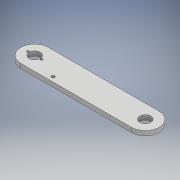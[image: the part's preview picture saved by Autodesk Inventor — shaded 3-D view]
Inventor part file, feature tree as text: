
AUTODESK INVENTOR PART (.ipt)
format: ipt  version: 2018.3 (Build 223284000, 284)  size: 119,808 bytes
history: native  units: mm
features: extrude x3, sketch x3
ambient origin geometry x8: Origin, YZ Plane, XZ Plane, XY Plane, X Axis, Y Axis, Z Axis, Center Point
bodies: Solid1 (feature_tree)
feature tree (6):
  extrude  "Extrusion1"  Depth=30.0mm
  extrude  "Extrusion2"  Depth=5.0mm TaperAngle=0.0deg
  extrude  "Extrusion3"  Depth=10.0mm
  sketch  "Sketch1"  dims[d0=12.0mm d1=30.0mm]
  sketch  "Sketch2"  dims[d2=120.0mm d4=5.0mm d5=0.0mm]
  sketch  "Sketch3"  dims[d6=120.0mm d9=12.0mm d10=3.5mm d11=5.0mm d13=12.0mm d14=0.0mm d15=30.0mm d16=14.8844mm d17=2.5mm d18=2.5mm d19=10.0mm d20=0.0mm]
